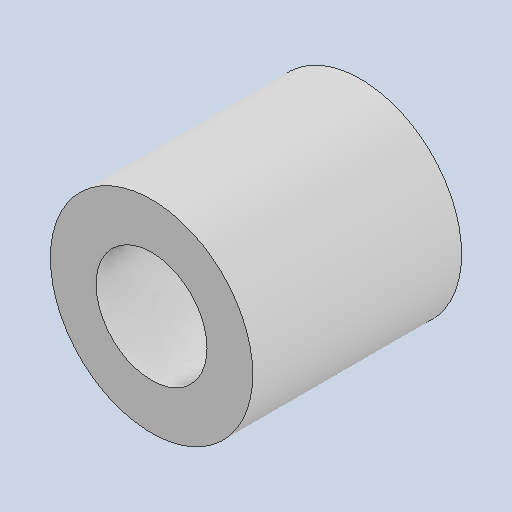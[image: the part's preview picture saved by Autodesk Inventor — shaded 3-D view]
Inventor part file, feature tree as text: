
AUTODESK INVENTOR PART (.ipt)
format: ipt  version: 2024 (Build 280153000, 153)  size: 101,888 bytes
history: native  units: in
note: dims shown in document units (in); Inventor stores cm internally (conversion verified against a paired STEP export)
features: extrude x1, sketch x1
ambient origin geometry x8: Origin, YZ Plane, XZ Plane, XY Plane, X Axis, Y Axis, Z Axis, Center Point
bodies: Solid1 (feature_tree)
feature tree (2):
  extrude  "Extrusion1"  Depth=0.32in
  sketch  "Sketch1"  dims[d0=0.17in d1=0.07in d2=0.32in d3=0.0in]
